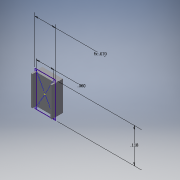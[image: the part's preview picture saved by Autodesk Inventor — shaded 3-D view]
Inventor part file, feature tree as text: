
AUTODESK INVENTOR PART (.ipt)
format: ipt  version: 2016 (Build 200138000, 138)  size: 101,888 bytes
history: native  units: in
note: dims shown in document units (in); Inventor stores cm internally (conversion verified against a paired STEP export)
features: extrude x2, sketch x1
ambient origin geometry x8: Origin, YZ Plane, XZ Plane, XY Plane, X Axis, Y Axis, Z Axis, Center Point
bodies: Solid1 (feature_tree)
feature tree (3):
  sketch  "Sketch2"  dims[d0=0.1181in d1=0.07in d2=0.025in d3=0.0in d6=0.06in d7=0.0125in d8=0.0in]
  extrude  "Extrusion1"  Depth=0.07in
  extrude  "Extrusion2"  Depth=0.025in TaperAngle=0.0deg
